# Revit family: HARMANN - BFDC_2022
name_source: partatom
category: Akcesoria wentylacyjne
units: mm (PartAtom-declared; Revit-internal decimal feet)

## family parameters
Oparty na płaszczyźnie roboczej = Nie
Tnij formami wycięć po wczytaniu = Nie
Typ części = Dzieli na
Współdzielony = Nie
Wymiar okrągłego złącza = Użyj średnicy
Zawsze pionowo = Tak

## types (12) — shared parameters
D = 260 mm
Opis = Przeciwpożarowa klapa odcinająca BFDC
d = 100 mm  [stored 0.328084 ft]
zero-valued in all types: Domyślna rzędna

## per-type parameters (varying)
| type | (Dn/2)-5.5 | Dn | Dn+2 | Dn-65.5 | Model | Opis indeksowy | Producent |
| BFDC 100 EI 120S | 45 mm | 100 mm  [stored 0.328084 ft] | 102 mm | 35 mm | BFDC-100-EI120S | BFDC-100-EI120S | Harmann Polska Sp. z o.o. |
| BFDC 160 EI 120S | 75 mm | 160 mm  [stored 0.524934 ft] | 162 mm | 95 mm | BFDC-160-EI120S | BFDC-160-EI120S | Harmann Polska Sp. z o.o. |
| BFDC 200 EI 60S | 95 mm | 200 mm  [stored 0.656168 ft] | 202 mm | 135 mm | BFDC-200-EI60S | BFDC-200-EI60S | Harmann Polska Sp. z o.o. |
| BFDC 200 EI 90S | 95 mm | 200 mm  [stored 0.656168 ft] | 202 mm | 135 mm | BFDC-200-EI90S | BFDC-200-EI90S |  |
| BFDC 200 EI 120S | 95 mm | 200 mm  [stored 0.656168 ft] | 202 mm | 135 mm | BFDC-200-EI120S | BFDC-200-EI120S | Harmann Polska Sp. z o.o. |
| BFDC 160 EI 90S | 75 mm | 160 mm  [stored 0.524934 ft] | 162 mm | 95 mm | BFDC-160-EI90S | BFDC-160-EI90S | Harmann Polska Sp. z o.o. |
| BFDC 160 EI 60S | 75 mm | 160 mm  [stored 0.524934 ft] | 162 mm | 95 mm | BFDC-160-EI60S | BFDC-160-EI60S | Harmann Polska Sp. z o.o. |
| BFDC 125 EI 60S | 57 mm | 125 mm  [stored 0.410105 ft] | 127 mm | 60 mm  [stored 0.19685 ft] | BFDC-125-EI60S | BFDC-125-EI60S | Harmann Polska Sp. z o.o. |
| BFDC 125 EI 90S | 57 mm | 125 mm  [stored 0.410105 ft] | 127 mm | 60 mm  [stored 0.19685 ft] | BFDC-125-EI90S | BFDC-125-EI90S | Harmann Polska Sp. z o.o. |
| BFDC 100 EI 60S | 45 mm | 100 mm  [stored 0.328084 ft] | 102 mm | 35 mm | BFDC-100-EI60S | BFDC-100-EI60S | Harmann Polska Sp. z o.o. |
| BFDC 100 EI 90S | 45 mm | 100 mm  [stored 0.328084 ft] | 102 mm | 35 mm | BFDC-100-EI90S | BFDC-100-EI90S | Harmann Polska Sp. z o.o. |
| BFDC 125 EI 120S | 57 mm | 125 mm  [stored 0.410105 ft] | 127 mm | 60 mm  [stored 0.19685 ft] | BFDC-125-EI120S | BFDC-125-EI120S | Harmann Polska Sp. z o.o. |

note: [stored X ft] marks values corroborated as IEEE doubles in the binary element streams (Revit-internal decimal feet)

## geometry (parser evidence)
native form markers: Sweep x5
no freeform markers — native parametric forms only
